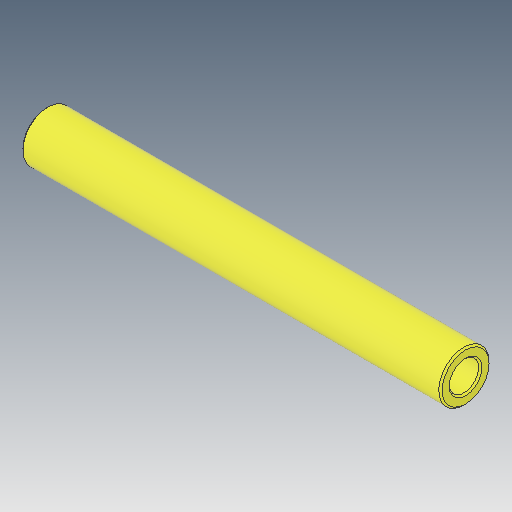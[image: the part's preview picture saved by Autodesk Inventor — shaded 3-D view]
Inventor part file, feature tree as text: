
AUTODESK INVENTOR PART (.ipt)
format: ipt  version: 2019.4 (Build 234330000, 330)  size: 102,912 bytes
history: native  units: mm
features: other x1, extrude x1, chamfer x1, sketch x1
ambient origin geometry x8: Origin, YZ Plane, XZ Plane, XY Plane, X Axis, Y Axis, Z Axis, Center Point
bodies: Body1 (feature_tree)
feature tree (4):
  other  "ソリッド1"
  extrude  "押し出し1"  Depth=6.0mm
  chamfer  "面取り1"  Distance=50.0mm
  sketch  "スケッチ1"
